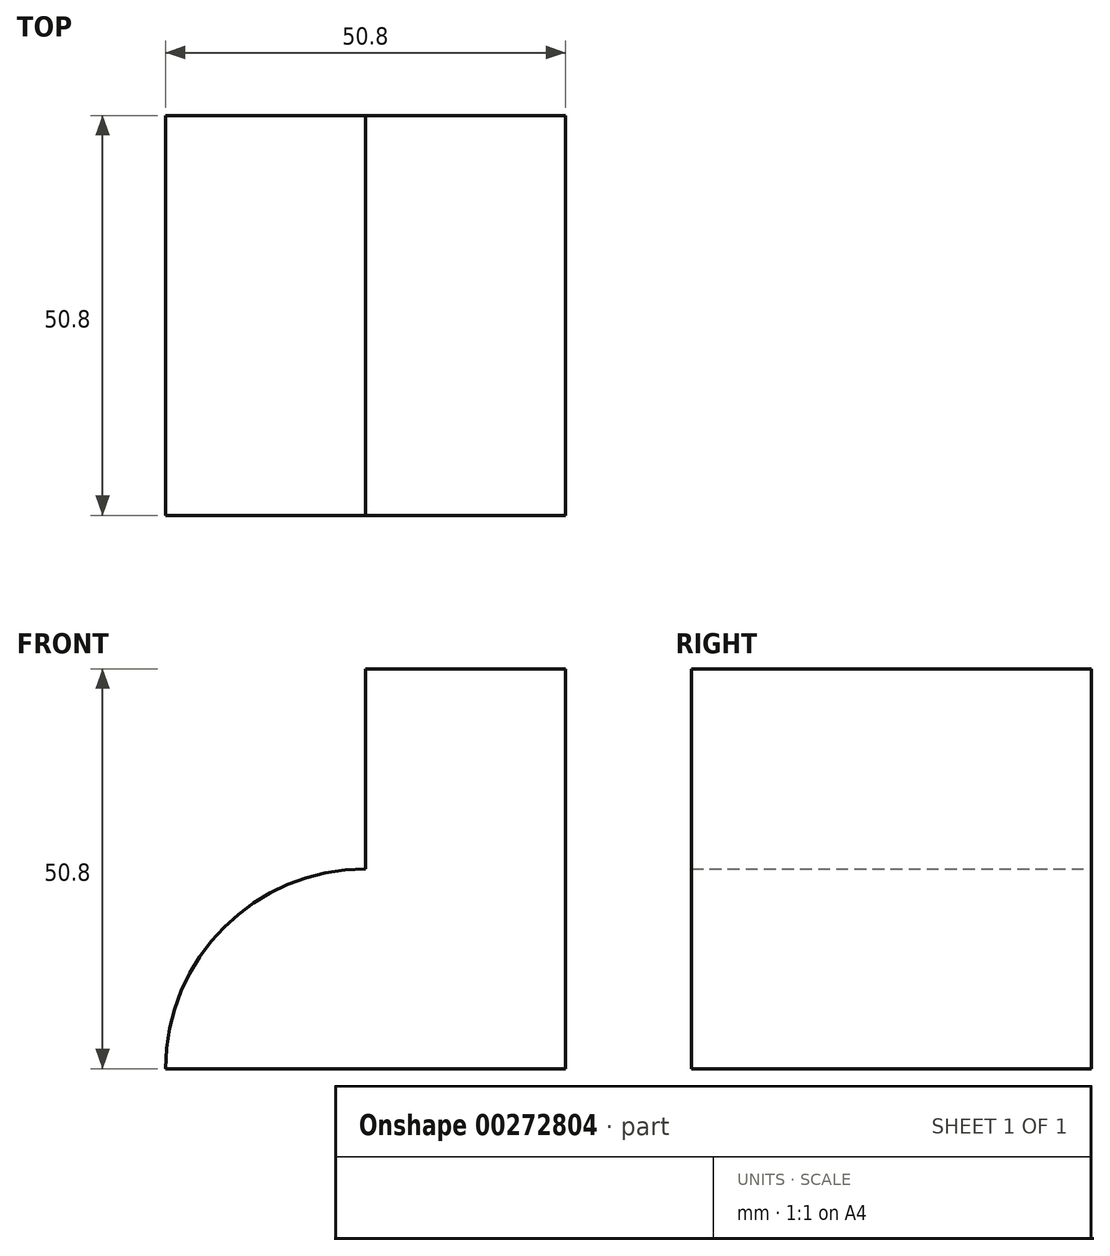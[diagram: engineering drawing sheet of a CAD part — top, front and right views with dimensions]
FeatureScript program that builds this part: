
annotation { "Feature Type Name" : "Feature", "Feature Type Description" : "" }
export const myFeature = defineFeature(function(context is Context, id is Id, definition is map)
    precondition{}
    {
        {
            var Q0;
            Q0=qCreatedBy(makeId("Front.planeOp"),FACE);
            var sketch = newSketch(context, id + "F0", { "sketchPlane" : qUnion([Q0])});
            skLineSegment(sketch, "E0", {"start": v(0, 0) * mm, "end": v(0, 50.8) * mm});
            skLineSegment(sketch, "E1", {"start": v(0, 0) * mm, "end": v(-50.8, 0) * mm});
            skLineSegment(sketch, "E2", {"start": v(0, 50.8) * mm, "end": v(-25.4, 50.8) * mm});
            skArc(sketch, "E3", {"start": v(-25.4, 25.4) * mm, "mid": v(-43.36, 17.96) * mm, "end": v(-50.8, 0) * mm});
            skLineSegment(sketch, "E4", {"start": v(-25.4, 50.8) * mm, "end": v(-25.4, 25.4) * mm});
            skSolve(sketch);
        }
        {
            var Q0;
            Q0 = qSketchRegion(id + "F0", true);
            extrude(context, id + "F1", {"entities" : qUnion([Q0]), "depth" : 50.8 * mm});
        }
    });
